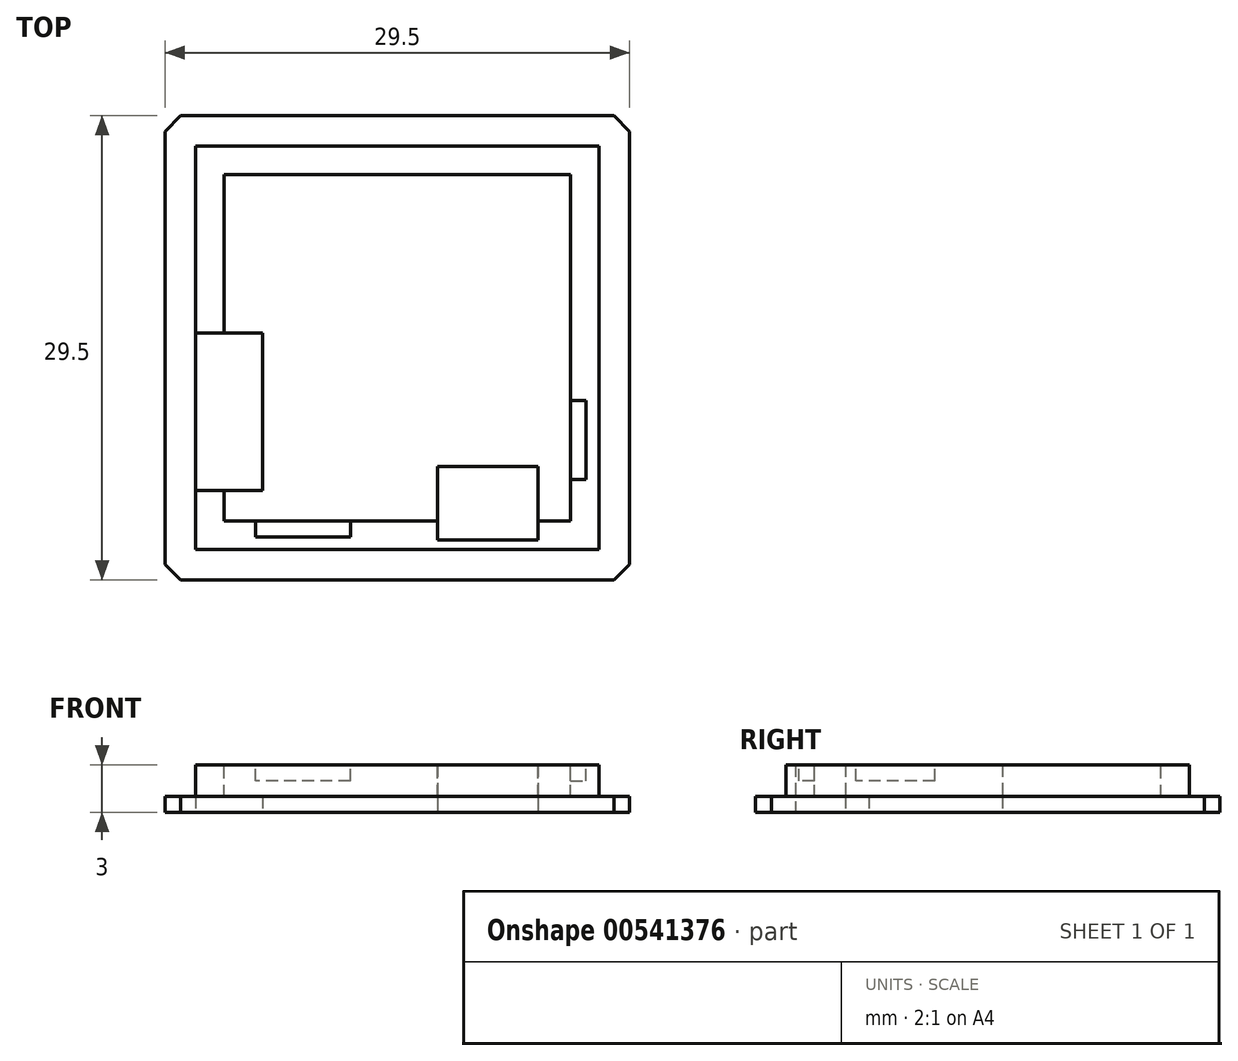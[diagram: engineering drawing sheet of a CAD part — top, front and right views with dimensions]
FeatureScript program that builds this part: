
annotation { "Feature Type Name" : "Feature", "Feature Type Description" : "" }
export const myFeature = defineFeature(function(context is Context, id is Id, definition is map)
    precondition{}
    {
        {
            var Q0;
            Q0=qCreatedBy(makeId("Top.planeOp"),FACE);
            var sketch = newSketch(context, id + "F0", { "sketchPlane" : qUnion([Q0])});
            skLineSegment(sketch, "E0.bottom", {"start": v(14.75, 14.75) * mm, "end": v(-14.75, 14.75) * mm});
            skLineSegment(sketch, "E0.top", {"start": v(14.75, -14.75) * mm, "end": v(-14.75, -14.75) * mm});
            skLineSegment(sketch, "E0.left", {"start": v(14.75, 14.75) * mm, "end": v(14.75, -14.75) * mm});
            skLineSegment(sketch, "E0.right", {"start": v(-14.75, 14.75) * mm, "end": v(-14.75, -14.75) * mm});
            skPoint(sketch, "E0.middle", {"position": v(0, 0) * mm});
            skLineSegment(sketch, "E1.bottom", {"start": v(12.8, 12.8) * mm, "end": v(-12.8, 12.8) * mm});
            skLineSegment(sketch, "E1.top", {"start": v(12.8, -12.8) * mm, "end": v(-12.8, -12.8) * mm});
            skLineSegment(sketch, "E1.left", {"start": v(12.8, 12.8) * mm, "end": v(12.8, -12.8) * mm});
            skLineSegment(sketch, "E1.right", {"start": v(-12.8, 12.8) * mm, "end": v(-12.8, -12.8) * mm});
            skLineSegment(sketch, "E2.MirrorCS", {"start": v(-12.8, 0.95) * mm, "end": v(-8.65, 0.95) * mm});
            skLineSegment(sketch, "E3.MirrorCS", {"start": v(-8.55, 0.95) * mm, "end": v(-8.55, -9.05) * mm});
            skLineSegment(sketch, "E4.MirrorCS", {"start": v(-12.8, -9.05) * mm, "end": v(-8.65, -9.05) * mm});
            skLineSegment(sketch, "E5.MirrorCS", {"start": v(8.95, -7.55) * mm, "end": v(2.55, -7.55) * mm});
            skLineSegment(sketch, "E6.MirrorCS", {"start": v(8.95, -12.2) * mm, "end": v(8.95, -7.55) * mm});
            skPoint(sketch, "E7.orphan", {"position": v(12.8, -9.05) * mm});
            skPoint(sketch, "E8.start.orphan", {"position": v(12.8, 0.95) * mm});
            skLineSegment(sketch, "E9", {"start": v(2.55, -12.2) * mm, "end": v(8.95, -12.2) * mm});
            skLineSegment(sketch, "E10.trimOffspring", {"start": v(2.55, -12.2) * mm, "end": v(2.55, -7.64) * mm});
            skPoint(sketch, "E11.orphan", {"position": v(8.95, -12.6) * mm});
            skLineSegment(sketch, "E12", {"start": v(2.55, -7.55) * mm, "end": v(2.55, -7.64) * mm});
            skLineSegment(sketch, "E13", {"start": v(-8.55, 0.95) * mm, "end": v(-8.65, 0.95) * mm});
            skLineSegment(sketch, "E14", {"start": v(-8.55, -9.05) * mm, "end": v(-8.65, -9.05) * mm});
            skSolve(sketch);
        }
        {
            var Q0;
            {var subQ5=sQuery(id+"F0.wireOp",EDGE,"E1.bottom");Q0=makeQuery(id+"F0.imprint","IMPRINT",FACE,{"disambiguationData":[TD([[makeQuery(id+"F0.imprint","IMPRINT",EDGE,{"derivedFrom":subQ5}),1.0]])]});}
            extrude(context, id + "F1", {"entities" : qUnion([Q0]), "depth" : 3.5 * mm, "offsetDistance" : 25 * mm});
        }
        {
            var Q0;
            Q0=makeQuery(id+"F0.imprint","IMPRINT",FACE,{"disambiguationData":[TD([[makeQuery(id+"F0.imprint","IMPRINT",EDGE,{"derivedFrom":sQuery(id+"F0.wireOp",EDGE,"E0.bottom")}),1.0]])]});
            extrude(context, id + "F2", {"entities" : qUnion([Q0]), "operationType" : NewBodyOperationType.ADD, "depth" : 1 * mm, "offsetDistance" : 25 * mm});
        }
        {
            var Q0;
            Q0=makeQuery(id+"F2.opExtrude","SWEPT_EDGE",EDGE,{"disambiguationData":[OSD([sQuery(id+"F0.wireOp",EDGE,"E0.bottom"),sQuery(id+"F0.wireOp",EDGE,"E0.left")])]});
            var Q1;
            Q1=makeQuery(id+"F2.opExtrude","SWEPT_EDGE",EDGE,{"disambiguationData":[OSD([sQuery(id+"F0.wireOp",EDGE,"E0.top"),sQuery(id+"F0.wireOp",EDGE,"E0.left")])]});
            var Q2;
            Q2=makeQuery(id+"F2.opExtrude","SWEPT_EDGE",EDGE,{"disambiguationData":[OSD([sQuery(id+"F0.wireOp",EDGE,"E0.top"),sQuery(id+"F0.wireOp",EDGE,"E0.right")])]});
            var Q3;
            Q3=makeQuery(id+"F2.opExtrude","SWEPT_EDGE",EDGE,{"disambiguationData":[OSD([sQuery(id+"F0.wireOp",EDGE,"E0.bottom"),sQuery(id+"F0.wireOp",EDGE,"E0.right")])]});
            chamfer(context, id + "F3", {"entities" : qUnion([Q0, Q1, Q2, Q3]), "width" : 1 * mm, "tangentPropagation" : true});
        }
        {
            var Q0;
            Q0=makeQuery(id+"F1.opExtrude","CAP_FACE",FACE,{"disambiguationData":[OSD([sQuery(id+"F0.wireOp",EDGE,"E1.bottom"),sQuery(id+"F0.wireOp",EDGE,"E1.top"),sQuery(id+"F0.wireOp",EDGE,"E1.left"),sQuery(id+"F0.wireOp",EDGE,"E1.right"),sQuery(id+"F0.wireOp",EDGE,"E2.MirrorCS"),sQuery(id+"F0.wireOp",EDGE,"E3.MirrorCS"),sQuery(id+"F0.wireOp",EDGE,"E4.MirrorCS"),sQuery(id+"F0.wireOp",EDGE,"E5.MirrorCS"),sQuery(id+"F0.wireOp",EDGE,"E6.MirrorCS"),sQuery(id+"F0.wireOp",EDGE,"7245e56b-ac51-46c6-bfb5-22646e07a0b40.MirrorCS")])],"isStart":false});
            var sketch = newSketch(context, id + "F4", { "sketchPlane" : qUnion([Q0])});
            skLineSegment(sketch, "E15.bottom", {"start": v(11, 11) * mm, "end": v(-11, 11) * mm});
            skLineSegment(sketch, "E15.top", {"start": v(11, -11) * mm, "end": v(-11, -11) * mm});
            skLineSegment(sketch, "E15.left", {"start": v(11, 11) * mm, "end": v(11, -11) * mm});
            skLineSegment(sketch, "E15.right", {"start": v(-11, 11) * mm, "end": v(-11, -11) * mm});
            skPoint(sketch, "E15.middle", {"position": v(0, 0) * mm});
            skSolve(sketch);
        }
        {
            var Q0;
            {var subQ8=sQuery(id+"F4.wireOp",EDGE,"E15.bottom");Q0=makeQuery(id+"F4.imprint","IMPRINT",FACE,{"disambiguationData":[TD([[makeQuery(id+"F4.imprint","IMPRINT",EDGE,{"derivedFrom":subQ8}),1.0]])]});}
            extrude(context, id + "F5", {"entities" : qUnion([Q0]), "operationType" : NewBodyOperationType.REMOVE, "oppositeDirection" : true, "depth" : 2.5 * mm, "offsetDistance" : 25 * mm});
        }
        {
            var Q0;
            Q0=makeQuery(id+"F1.opExtrude","CAP_FACE",FACE,{"disambiguationData":[OSD([sQuery(id+"F0.wireOp",EDGE,"E1.bottom"),sQuery(id+"F0.wireOp",EDGE,"E1.top"),sQuery(id+"F0.wireOp",EDGE,"E1.left"),sQuery(id+"F0.wireOp",EDGE,"E1.right"),sQuery(id+"F0.wireOp",EDGE,"E2.MirrorCS"),sQuery(id+"F0.wireOp",EDGE,"E3.MirrorCS"),sQuery(id+"F0.wireOp",EDGE,"E4.MirrorCS"),sQuery(id+"F0.wireOp",EDGE,"E5.MirrorCS"),sQuery(id+"F0.wireOp",EDGE,"E6.MirrorCS"),sQuery(id+"F0.wireOp",EDGE,"E9"),sQuery(id+"F0.wireOp",EDGE,"E10.trimOffspring"),sQuery(id+"F0.wireOp",EDGE,"E12"),sQuery(id+"F0.wireOp",EDGE,"E13"),sQuery(id+"F0.wireOp",EDGE,"E14")])],"isStart":false});
            var sketch = newSketch(context, id + "F6", { "sketchPlane" : qUnion([Q0])});
            skLineSegment(sketch, "E16", {"start": v(11, -8.36) * mm, "end": v(12, -8.36) * mm});
            skLineSegment(sketch, "E17", {"start": v(12, -8.36) * mm, "end": v(12, -3.36) * mm});
            skLineSegment(sketch, "E18", {"start": v(12, -3.36) * mm, "end": v(11, -3.36) * mm});
            skLineSegment(sketch, "E19", {"start": v(-8.98, -11) * mm, "end": v(-8.98, -12) * mm});
            skLineSegment(sketch, "E20", {"start": v(-8.98, -12) * mm, "end": v(-2.98, -12) * mm});
            skLineSegment(sketch, "E21", {"start": v(-2.98, -12) * mm, "end": v(-2.98, -11) * mm});
            skSolve(sketch);
        }
        {
            var Q0;
            {var subQ0=sQuery(id+"F6.wireOp",EDGE,"E16");Q0=makeQuery(id+"F6.imprint","IMPRINT",FACE,{"disambiguationData":[TD([[makeQuery(id+"F6.imprint","IMPRINT",EDGE,{"derivedFrom":subQ0}),1.0]])]});}
            var Q1;
            {var subQ0=sQuery(id+"F6.wireOp",EDGE,"E19");Q1=makeQuery(id+"F6.imprint","IMPRINT",FACE,{"disambiguationData":[TD([[makeQuery(id+"F6.imprint","IMPRINT",EDGE,{"derivedFrom":subQ0}),1.0]])]});}
            extrude(context, id + "F7", {"entities" : qUnion([Q0, Q1]), "operationType" : NewBodyOperationType.REMOVE, "oppositeDirection" : true, "depth" : 1.5 * mm, "offsetDistance" : 25 * mm});
        }
        {
            var Q0;
            Q0=makeQuery(id+"F1.opExtrude","CAP_FACE",FACE,{"disambiguationData":[OSD([sQuery(id+"F0.wireOp",EDGE,"E1.bottom"),sQuery(id+"F0.wireOp",EDGE,"E1.top"),sQuery(id+"F0.wireOp",EDGE,"E1.left"),sQuery(id+"F0.wireOp",EDGE,"E1.right"),sQuery(id+"F0.wireOp",EDGE,"E2.MirrorCS"),sQuery(id+"F0.wireOp",EDGE,"E3.MirrorCS"),sQuery(id+"F0.wireOp",EDGE,"E4.MirrorCS"),sQuery(id+"F0.wireOp",EDGE,"E5.MirrorCS"),sQuery(id+"F0.wireOp",EDGE,"E6.MirrorCS"),sQuery(id+"F0.wireOp",EDGE,"E9"),sQuery(id+"F0.wireOp",EDGE,"E10.trimOffspring"),sQuery(id+"F0.wireOp",EDGE,"E12"),sQuery(id+"F0.wireOp",EDGE,"E13"),sQuery(id+"F0.wireOp",EDGE,"E14")])],"isStart":false});
            extrude(context, id + "F8", {"entities" : qUnion([Q0]), "operationType" : NewBodyOperationType.REMOVE, "oppositeDirection" : true, "depth" : 0.5 * mm, "offsetDistance" : 25 * mm});
        }
    });
